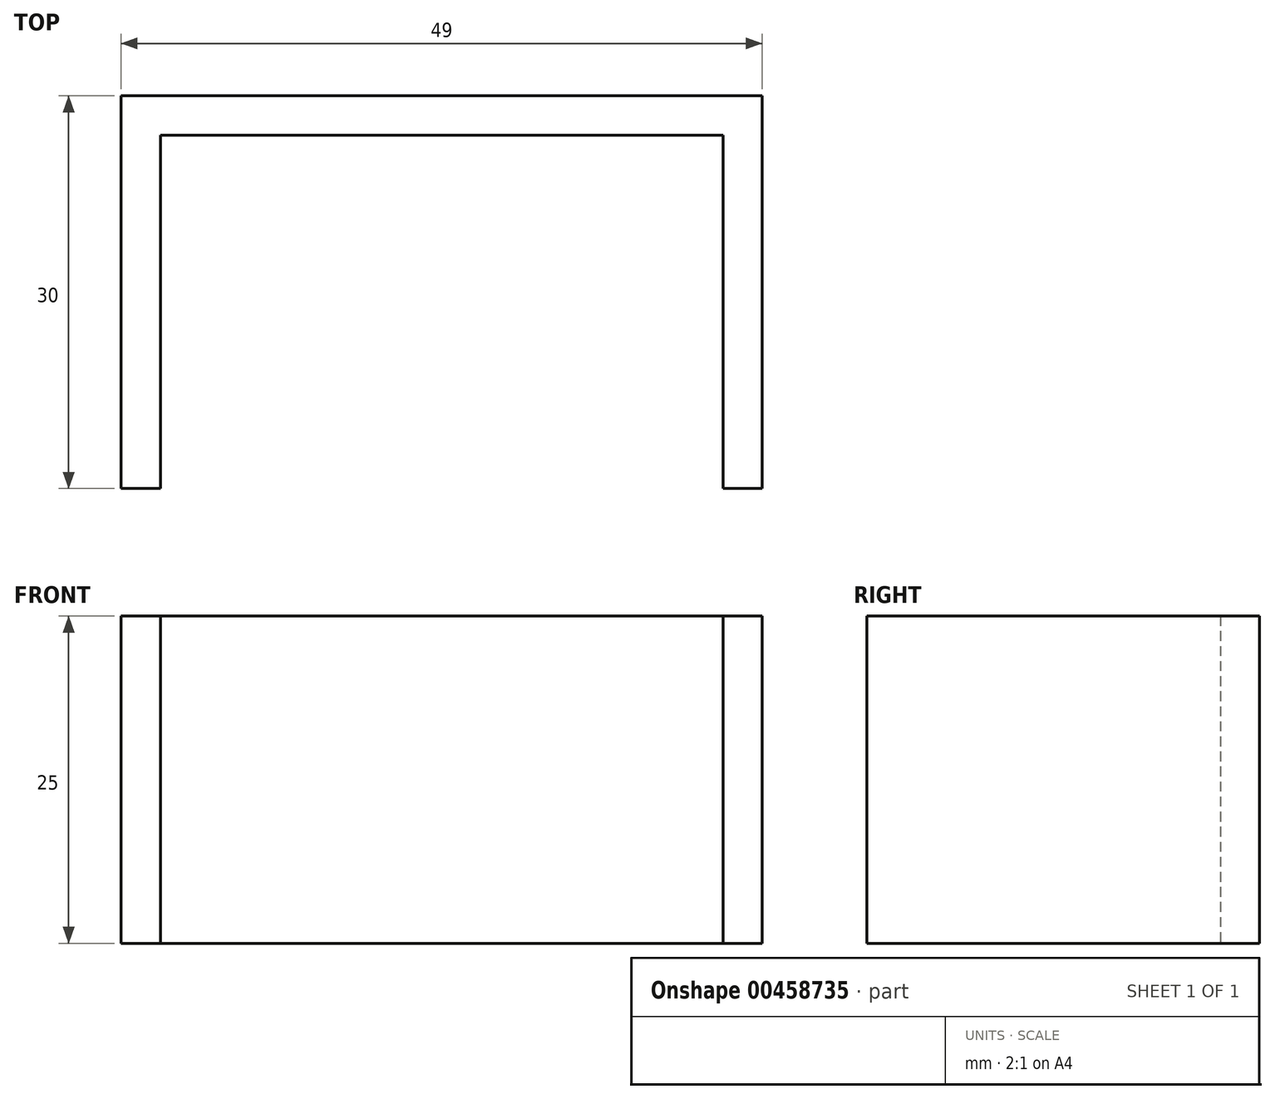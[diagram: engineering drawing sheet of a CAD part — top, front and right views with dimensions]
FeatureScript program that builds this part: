
annotation { "Feature Type Name" : "Feature", "Feature Type Description" : "" }
export const myFeature = defineFeature(function(context is Context, id is Id, definition is map)
    precondition{}
    {
        {
            var Q0;
            Q0=qCreatedBy(makeId("Top.planeOp"),FACE);
            var sketch = newSketch(context, id + "F0", { "sketchPlane" : qUnion([Q0])});
            skLineSegment(sketch, "E0.bottom", {"start": v(-12.46, 16.23) * mm, "end": v(30.54, 16.23) * mm});
            skLineSegment(sketch, "E0.top", {"start": v(-12.46, 13.23) * mm, "end": v(30.54, 13.23) * mm});
            skLineSegment(sketch, "E0.left", {"start": v(-12.46, 16.23) * mm, "end": v(-12.46, 13.23) * mm});
            skLineSegment(sketch, "E0.right", {"start": v(30.54, 16.23) * mm, "end": v(30.54, 13.23) * mm});
            skLineSegment(sketch, "E1.bottom", {"start": v(30.54, 16.23) * mm, "end": v(33.54, 16.23) * mm});
            skLineSegment(sketch, "E1.top", {"start": v(30.54, -13.77) * mm, "end": v(33.54, -13.77) * mm});
            skLineSegment(sketch, "E1.left", {"start": v(30.54, 16.23) * mm, "end": v(30.54, -13.77) * mm});
            skLineSegment(sketch, "E1.right", {"start": v(33.54, 16.23) * mm, "end": v(33.54, -13.77) * mm});
            skLineSegment(sketch, "E2.bottom", {"start": v(-12.46, 16.23) * mm, "end": v(-15.46, 16.23) * mm});
            skLineSegment(sketch, "E2.top", {"start": v(-12.46, -13.77) * mm, "end": v(-15.46, -13.77) * mm});
            skLineSegment(sketch, "E2.left", {"start": v(-12.46, 16.23) * mm, "end": v(-12.46, -13.77) * mm});
            skLineSegment(sketch, "E2.right", {"start": v(-15.46, 16.23) * mm, "end": v(-15.46, -13.77) * mm});
            skSolve(sketch);
        }
        {
            var Q0;
            Q0 = qSketchRegion(id + "F0", true);
            extrude(context, id + "F1", {"entities" : qUnion([Q0]), "depth" : 25 * mm, "offsetDistance" : 25 * mm});
        }
        {
            var Q0;
            Q0=qCreatedBy(makeId("Front.planeOp"),FACE);
            cPlane(context, id + "F2", {"entities" : qUnion([Q0]), "cplaneType" : CPlaneType.OFFSET, "offset" : 10 * mm, "width" : 150 * mm, "height" : 150 * mm});
        }
    });
